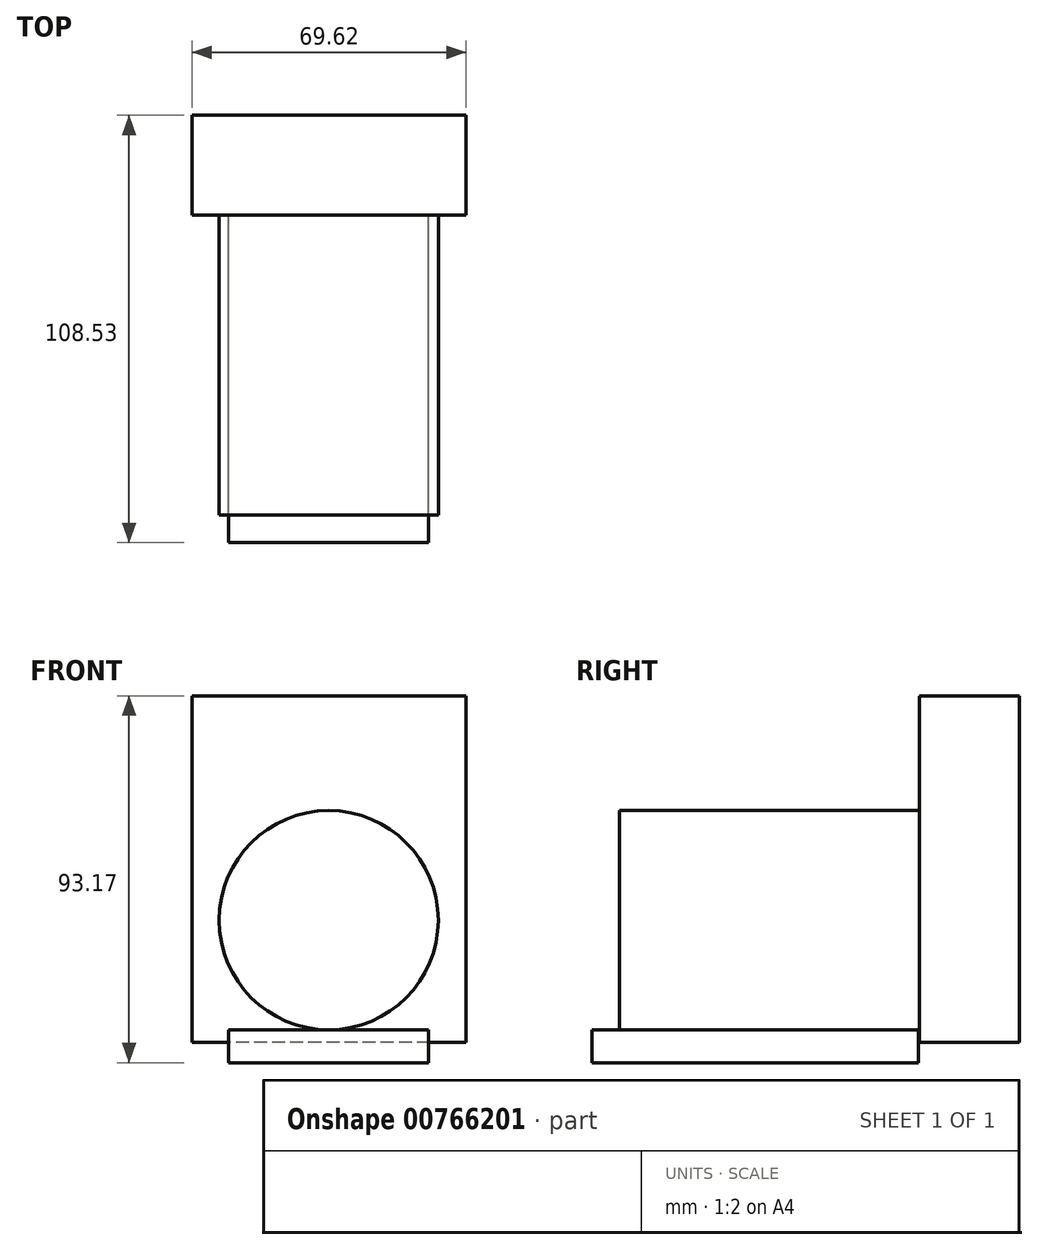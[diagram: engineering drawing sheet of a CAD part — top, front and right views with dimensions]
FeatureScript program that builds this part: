
annotation { "Feature Type Name" : "Feature", "Feature Type Description" : "" }
export const myFeature = defineFeature(function(context is Context, id is Id, definition is map)
    precondition{}
    {
        {
            var Q0;
            Q0=qCreatedBy(makeId("Front.planeOp"),FACE);
            var sketch = newSketch(context, id + "F0", { "sketchPlane" : qUnion([Q0])});
            skCircle(sketch, "E0", {"center": v(0, 0) * mm, "radius": 27.84 * mm});
            skSolve(sketch);
        }
        {
            var Q0;
            Q0=makeQuery(id+"F0.imprint","IMPRINT",FACE,{"disambiguationData":[TD([[makeQuery(id+"F0.imprint","IMPRINT",EDGE,{"derivedFrom":sQuery(id+"F0.wireOp",EDGE,"E0")}),1.0]])]});
            extrude(context, id + "F1", {"entities" : qUnion([Q0]), "depth" : 101.6 * mm, "offsetDistance" : 25.4 * mm});
        }
        {
            var Q0;
            Q0=qCreatedBy(makeId("Front.planeOp"),FACE);
            var sketch = newSketch(context, id + "F2", { "sketchPlane" : qUnion([Q0])});
            skLineSegment(sketch, "E1.bottom", {"start": v(34.91, -31.05) * mm, "end": v(-34.71, -31.05) * mm});
            skLineSegment(sketch, "E1.top", {"start": v(34.91, 56.97) * mm, "end": v(-34.71, 56.97) * mm});
            skLineSegment(sketch, "E1.left", {"start": v(34.91, -31.05) * mm, "end": v(34.91, 56.97) * mm});
            skLineSegment(sketch, "E1.right", {"start": v(-34.71, -31.05) * mm, "end": v(-34.71, 56.97) * mm});
            skSolve(sketch);
        }
        {
            var Q0;
            Q0=makeQuery(id+"F2.imprint","IMPRINT",FACE,{"disambiguationData":[TD([[makeQuery(id+"F2.imprint","IMPRINT",EDGE,{"derivedFrom":sQuery(id+"F2.wireOp",EDGE,"E1.bottom")}),-1.0]])]});
            extrude(context, id + "F3", {"entities" : qUnion([Q0]), "operationType" : NewBodyOperationType.ADD, "depth" : 25.4 * mm, "offsetDistance" : 25.4 * mm});
        }
        {
            var Q0;
            Q0=qCreatedBy(makeId("Right.planeOp"),FACE);
            var sketch = newSketch(context, id + "F4", { "sketchPlane" : qUnion([Q0])});
            skLineSegment(sketch, "E2.bottom", {"start": v(-108.53, -27.89) * mm, "end": v(-25.66, -27.89) * mm});
            skLineSegment(sketch, "E2.top", {"start": v(-108.53, -36.2) * mm, "end": v(-25.66, -36.2) * mm});
            skLineSegment(sketch, "E2.left", {"start": v(-108.53, -27.89) * mm, "end": v(-108.53, -36.2) * mm});
            skLineSegment(sketch, "E2.right", {"start": v(-25.66, -27.89) * mm, "end": v(-25.66, -36.2) * mm});
            skSolve(sketch);
        }
        {
            var Q0;
            Q0=makeQuery(id+"F4.imprint","IMPRINT",FACE,{"disambiguationData":[TD([[makeQuery(id+"F4.imprint","IMPRINT",EDGE,{"derivedFrom":sQuery(id+"F4.wireOp",EDGE,"E2.bottom")}),-1.0]])]});
            extrude(context, id + "F5", {"entities" : qUnion([Q0]), "depth" : 25.4 * mm, "offsetDistance" : 25.4 * mm});
        }
        {
            var Q0;
            Q0=makeQuery(id+"F5.opExtrude","CAP_FACE",FACE,{"disambiguationData":[OSD([sQuery(id+"F4.wireOp",EDGE,"E2.bottom"),sQuery(id+"F4.wireOp",EDGE,"E2.top"),sQuery(id+"F4.wireOp",EDGE,"E2.left"),sQuery(id+"F4.wireOp",EDGE,"E2.right")])],"isStart":true});
            extrude(context, id + "F6", {"entities" : qUnion([Q0]), "operationType" : NewBodyOperationType.ADD, "depth" : 25.4 * mm, "offsetDistance" : 25.4 * mm});
        }
        {
            var Q0;
            Q0=qCreatedBy(makeId("Top.planeOp"),FACE);
            var sketch = newSketch(context, id + "F7", { "sketchPlane" : qUnion([Q0])});
            skCircle(sketch, "E3", {"center": v(0, -87.86) * mm, "radius": 8.31 * mm});
            skSolve(sketch);
        }
        {
            var Q0;
            Q0=sQuery(id+"F7.wireOp",EDGE,"E3");
            extrude(context, id + "F8", {"bodyType" : ToolBodyType.SURFACE, "surfaceEntities" : qUnion([Q0]), "depth" : 50.8 * mm, "offsetDistance" : 25.4 * mm});
        }
    });
